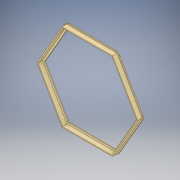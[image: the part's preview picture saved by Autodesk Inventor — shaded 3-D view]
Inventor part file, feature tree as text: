
AUTODESK INVENTOR PART (.ipt)
format: ipt  version: 2019 (Build 230136000, 136)  size: 152,576 bytes
history: native  units: mm
features: extrude x3, sketch x3, projected_geometry x2, fillet x1
ambient origin geometry x8: Origin, YZ Plane, XZ Plane, XY Plane, X Axis, Y Axis, Z Axis, Center Point
bodies: Solid1 (feature_tree)
feature tree (9):
  extrude  "Extrusion1"  Depth=2.0mm TaperAngle=0.0deg
  extrude  "Extrusion5"  Depth=2.0mm
  extrude  "Extrusion6"  Depth=4.0mm
  fillet  "Fillet1"  Radius=7.0mm
  sketch  "Sketch1"  dims[d0=200.0mm d1=2.0mm d2=0.0mm]
  sketch  "Sketch5"  dims[d15=2.0mm d16=2.0mm]
  projected_geometry  "Projected Loop4"
  sketch  "Sketch7"  dims[d17=10.0mm d18=0.0mm d19=4.0mm d20=7.0mm d21=0.0mm d22=10.0mm]
  projected_geometry  "Projected Loop6"
